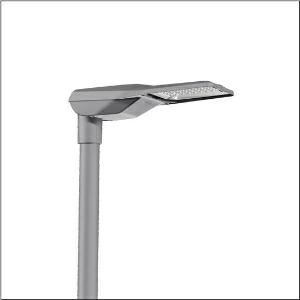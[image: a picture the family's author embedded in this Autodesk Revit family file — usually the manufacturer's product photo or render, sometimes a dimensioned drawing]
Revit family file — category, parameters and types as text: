
# Revit family: streetlight_sl_21_iq_mini___p1_0a_5xe2a41g08hb_15d1
name_source: partatom
category: Lighting Fixtures
units: mm (PartAtom-declared; Revit-internal decimal feet)

## family parameters
Cut with Voids When Loaded = No
Host = Face
Light Source = No
Part Type = Normal
Room Calculation Point = No
Round Connector Dimension = Use Diameter
Shared = No

## types (1)
- --- (1 x LED, 9860 lm, 70.9 W, 4000K)
    Apparent Load = 71 VA
    CIE Flux Codes = 21 50 90 100 100
    Color Rendering = 70
    Color Temperature = 4000K
    Default Elevation = 1800 mm
    Description = Streetlight SL 21 iQ mini, mast luminaire, primary light control with lens, of PMMA, primary optical cover: cover, of toughened safety glass, transparent, light distribution: P1.0a, light emission: direct distribution, primary light characteristic: asymmetric, installation type: post-top, side-entry, LED, High Power LED, rated luminous flux: 9.860lm, luminous efficacy: 139lm/W, light colour: 740, colour temperature: 4000K, control: Street-Remote, Auto-Match, Temp-Guard, Lumen-Switch, Night-Set, Smart-Wire, Light-Fading, Desk-Remote (wireless, voltage-free reading and setting of iQ features in the workshop via application-optimized NFC function/RFID function), optimised constant luminous flux control (CLO 2.0), presetting dimming linear, mains connection: 220..240V, AC, 50/60Hz, start of lifetime: 71W, end of service life: 75W, reduction: 31W, luminaire housing, of diecast aluminium, powder-coated, Siteco® metallic grey (DB 702S), corrosivity category C5 mid according to DIN EN ISO 12944, please order mast flange separately, inclination adjustable: 0°, 5°, 10°, 15°, sealing non-destructively replaceable, multi-level sealing system, length: 628mm, width: 235mm, height: 110mm, mast flange for spigot size: 42mm (side-entry): 5XC10008XM4, 60/48mm (side-entry/post-top): 5XC10108XM2, 76/60mm (side-entry/post-top): 5XC10108XM1, protection rating (complete): IP66, insulation class (complete): insulation class II (safety insulation), certification: CE, ENEC, ENEC+, VDE, impact resistance: IK09, permissible operating ambient temperature for outdoor applications: -40..+50°C, standard-compliant lighting for roads and squares, packaging unit: 1 piece

Light Distribution: P1.0a
    Height = 110 mm
    Lamp = 1 x LED
    Lamp Light Flux = 9860 lm
    Lamp Power = 70.9 W
    Lamp count = 1
    Length = 625 mm
    Luminous efficacy = 139 lm/W
    Manufacturer = Siteco
    ModVariant = No
    Model = 5XE2A41G08HB
    Number of Poles = 1
    OnlyDefault = Yes
    Power Factor = 1
    Product Name = Streetlight SL 21 iQ mini | P1.0a
    Product group = mast luminaire | pylon top
    ProductGroupID = 6100
    Protection Class = Protection class II
    Protection Degree = IP 66
    RLX_Detail_Level = 1
    RLX_Emergency_Light_Flux = 0 lm
    RLX_Emergency_Type = 0
    RLX_Emergency_Type_DB = No
    RlxData = <blob elided: 103761 chars, md5=90af8206>
    Socket = socket
    Standby Power = 0 W
    System Light Flux = 9860 lm
    System Power = 71 W
    Type Comments = factory setting: luminous flux: 100 % | dim-lin: 254 | 711 mA
    Type Image = l_1003519.jpg
    URL = http://relux.com
    VarID = @adj_107777
    Voltage = 0 V
    Weight = 0.00 kg
    Width = 234 mm

## geometry (parser evidence)
native form markers: Blend x4, Sweep x12
no freeform markers — native parametric forms only
